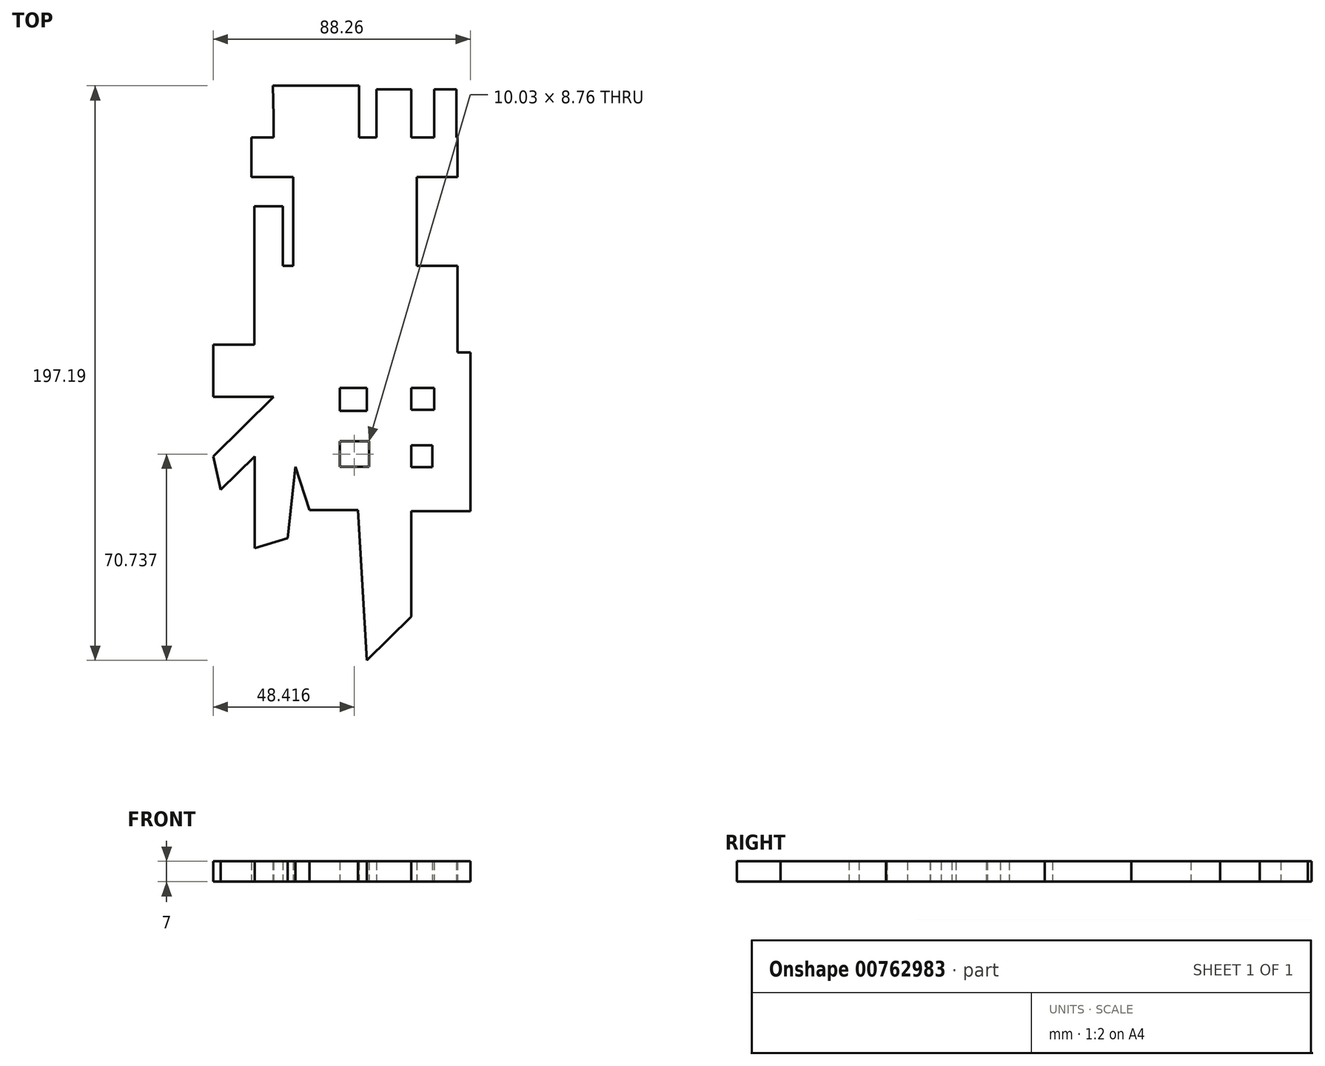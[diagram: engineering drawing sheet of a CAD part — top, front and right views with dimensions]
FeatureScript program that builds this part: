
annotation { "Feature Type Name" : "Feature", "Feature Type Description" : "" }
export const myFeature = defineFeature(function(context is Context, id is Id, definition is map)
    precondition{}
    {
        {
            var Q0;
            Q0=qCreatedBy(makeId("Top.planeOp"),FACE);
            var sketch = newSketch(context, id + "F0", { "sketchPlane" : qUnion([Q0])});
            skSolve(sketch);
        }
        {
            var Q0;
            Q0=qCreatedBy(makeId("Top.planeOp"),FACE);
            var sketch = newSketch(context, id + "F1", { "sketchPlane" : qUnion([Q0])});
            skLineSegment(sketch, "E0", {"start": v(-41.92, 16.1) * mm, "end": v(-3.32, 16.1) * mm});
            skLineSegment(sketch, "E1", {"start": v(-3.32, 16.1) * mm, "end": v(-3.32, 27.06) * mm});
            skLineSegment(sketch, "E2", {"start": v(-3.32, 27.06) * mm, "end": v(-14.67, 27.06) * mm});
            skLineSegment(sketch, "E3", {"start": v(-14.67, 27.06) * mm, "end": v(-14.67, 34.84) * mm});
            skLineSegment(sketch, "E4", {"start": v(-14.67, 34.84) * mm, "end": v(-3.32, 34.84) * mm});
            skLineSegment(sketch, "E5", {"start": v(-3.32, 34.84) * mm, "end": v(-3.32, 47.5) * mm});
            skLineSegment(sketch, "E6", {"start": v(-3.32, 47.5) * mm, "end": v(-14.67, 47.5) * mm});
            skLineSegment(sketch, "E7", {"start": v(-14.67, 47.5) * mm, "end": v(-14.67, 57.55) * mm});
            skLineSegment(sketch, "E8", {"start": v(-14.67, 57.55) * mm, "end": v(0, 57.55) * mm});
            skLineSegment(sketch, "E9", {"start": v(0, 57.55) * mm, "end": v(0, 16.1) * mm});
            skLineSegment(sketch, "E10", {"start": v(27.83, 18.3) * mm, "end": v(27.83, 27.06) * mm});
            skLineSegment(sketch, "E11", {"start": v(27.83, 27.06) * mm, "end": v(13.88, 27.06) * mm});
            skLineSegment(sketch, "E12", {"start": v(13.88, 27.06) * mm, "end": v(13.88, 57.55) * mm});
            skLineSegment(sketch, "E13", {"start": v(13.88, 57.55) * mm, "end": v(27.83, 57.55) * mm});
            skLineSegment(sketch, "E14", {"start": v(27.83, 57.55) * mm, "end": v(27.83, 71.18) * mm});
            skLineSegment(sketch, "E15", {"start": v(27.83, 71.18) * mm, "end": v(11.93, 71.18) * mm});
            skLineSegment(sketch, "E16", {"start": v(11.93, 71.18) * mm, "end": v(11.93, 87.72) * mm});
            skLineSegment(sketch, "E17", {"start": v(11.93, 87.72) * mm, "end": v(0, 87.72) * mm});
            skLineSegment(sketch, "E18", {"start": v(0, 87.72) * mm, "end": v(0, 71.18) * mm});
            skLineSegment(sketch, "E19", {"start": v(0, 71.18) * mm, "end": v(-42.9, 71.18) * mm});
            skLineSegment(sketch, "E20", {"start": v(-42.9, 71.18) * mm, "end": v(-42.9, 57.55) * mm});
            skLineSegment(sketch, "E21", {"start": v(-42.9, 57.55) * mm, "end": v(-28.62, 57.55) * mm});
            skLineSegment(sketch, "E22", {"start": v(-28.62, 57.55) * mm, "end": v(-28.62, 27.06) * mm});
            skLineSegment(sketch, "E23", {"start": v(-28.62, 27.06) * mm, "end": v(-32.19, 27.06) * mm});
            skLineSegment(sketch, "E24", {"start": v(-32.19, 27.06) * mm, "end": v(-32.19, 47.5) * mm});
            skLineSegment(sketch, "E25", {"start": v(-32.19, 47.5) * mm, "end": v(-41.92, 47.5) * mm});
            skLineSegment(sketch, "E26", {"start": v(-41.92, 47.5) * mm, "end": v(-41.92, 16.1) * mm});
            skLineSegment(sketch, "E27", {"start": v(0, 16.1) * mm, "end": v(27.83, 16.1) * mm});
            skLineSegment(sketch, "E28", {"start": v(27.83, 18.3) * mm, "end": v(27.83, 16.1) * mm});
            skLineSegment(sketch, "E29", {"start": v(-35.28, 78.46) * mm, "end": v(-6.02, 78.46) * mm});
            skLineSegment(sketch, "E30", {"start": v(-6.02, 78.46) * mm, "end": v(-6.02, 88.9) * mm});
            skLineSegment(sketch, "E31", {"start": v(-6.02, 88.9) * mm, "end": v(-35.63, 88.9) * mm});
            skLineSegment(sketch, "E32", {"start": v(19.76, 87.72) * mm, "end": v(19.76, 77.06) * mm});
            skLineSegment(sketch, "E33", {"start": v(19.76, 77.06) * mm, "end": v(27.42, 77.06) * mm});
            skLineSegment(sketch, "E34", {"start": v(27.42, 77.06) * mm, "end": v(27.42, 87.72) * mm});
            skLineSegment(sketch, "E35", {"start": v(27.42, 87.72) * mm, "end": v(19.76, 87.72) * mm});
            skLineSegment(sketch, "E36", {"start": v(-35.63, 88.9) * mm, "end": v(-35.28, 78.46) * mm});
            skLineSegment(sketch, "E37", {"start": v(-56.05, -17.86) * mm, "end": v(-35.28, -17.86) * mm});
            skLineSegment(sketch, "E38", {"start": v(-56.05, -38.25) * mm, "end": v(-35.28, -17.86) * mm});
            skLineSegment(sketch, "E39", {"start": v(-56.05, -38.25) * mm, "end": v(-53.45, -49.74) * mm});
            skLineSegment(sketch, "E40", {"start": v(-53.45, -49.74) * mm, "end": v(-41.75, -38.25) * mm});
            skLineSegment(sketch, "E41", {"start": v(-41.75, -38.25) * mm, "end": v(-41.75, -69.76) * mm});
            skLineSegment(sketch, "E42", {"start": v(-41.75, -69.76) * mm, "end": v(-30.47, -66.42) * mm});
            skLineSegment(sketch, "E43", {"start": v(-30.47, -66.42) * mm, "end": v(-27.84, -41.92) * mm});
            skLineSegment(sketch, "E44", {"start": v(-27.84, -41.92) * mm, "end": v(-23.03, -56.75) * mm});
            skLineSegment(sketch, "E45", {"start": v(-23.03, -56.75) * mm, "end": v(-6.35, -56.75) * mm});
            skLineSegment(sketch, "E46", {"start": v(-6.35, -56.75) * mm, "end": v(-3.32, -108.28) * mm});
            skLineSegment(sketch, "E47", {"start": v(-3.32, -108.28) * mm, "end": v(11.93, -93.3) * mm});
            skLineSegment(sketch, "E48", {"start": v(11.93, -93.3) * mm, "end": v(11.93, -57.12) * mm});
            skLineSegment(sketch, "E49", {"start": v(11.93, -57.12) * mm, "end": v(32.2, -57.12) * mm});
            skLineSegment(sketch, "E50", {"start": v(32.2, -57.12) * mm, "end": v(32.2, -2.63) * mm});
            skLineSegment(sketch, "E51", {"start": v(32.2, -2.63) * mm, "end": v(11.93, -2.63) * mm});
            skLineSegment(sketch, "E52", {"start": v(11.93, -2.63) * mm, "end": v(11.93, 12.57) * mm});
            skLineSegment(sketch, "E53", {"start": v(11.93, 12.57) * mm, "end": v(-3.32, 12.57) * mm});
            skLineSegment(sketch, "E54", {"start": v(-3.32, 12.57) * mm, "end": v(-3.32, 0) * mm});
            skLineSegment(sketch, "E55", {"start": v(-3.32, 0) * mm, "end": v(-56.05, 0) * mm});
            skLineSegment(sketch, "E56", {"start": v(-56.05, 0) * mm, "end": v(-56.05, -17.86) * mm});
            skLineSegment(sketch, "E57", {"start": v(-12.65, -14.86) * mm, "end": v(-12.65, -22.65) * mm});
            skLineSegment(sketch, "E58", {"start": v(-12.65, -22.65) * mm, "end": v(-3.32, -22.65) * mm});
            skLineSegment(sketch, "E59", {"start": v(-3.32, -22.65) * mm, "end": v(-3.32, -14.86) * mm});
            skLineSegment(sketch, "E60", {"start": v(-3.32, -14.86) * mm, "end": v(-12.65, -14.86) * mm});
            skLineSegment(sketch, "E61", {"start": v(-9.04, -41.92) * mm, "end": v(-3.32, -41.92) * mm});
            skLineSegment(sketch, "E62", {"start": v(-12.65, -34.51) * mm, "end": v(-12.65, -38.25) * mm});
            skLineSegment(sketch, "E63", {"start": v(11.93, -38.25) * mm, "end": v(11.93, -41.92) * mm});
            skLineSegment(sketch, "E64", {"start": v(11.93, -14.86) * mm, "end": v(11.93, -22.28) * mm});
            skLineSegment(sketch, "E65", {"start": v(11.93, -22.28) * mm, "end": v(19.76, -22.28) * mm});
            skLineSegment(sketch, "E66", {"start": v(19.76, -22.28) * mm, "end": v(19.76, -14.86) * mm});
            skLineSegment(sketch, "E67", {"start": v(19.76, -14.86) * mm, "end": v(11.93, -14.86) * mm});
            skLineSegment(sketch, "E68.bottom", {"start": v(-12.65, -33.16) * mm, "end": v(-2.62, -33.16) * mm});
            skLineSegment(sketch, "E68.top", {"start": v(-12.65, -41.92) * mm, "end": v(-2.62, -41.92) * mm});
            skLineSegment(sketch, "E68.left", {"start": v(-12.65, -33.16) * mm, "end": v(-12.65, -41.92) * mm});
            skLineSegment(sketch, "E68.right", {"start": v(-2.62, -33.16) * mm, "end": v(-2.62, -41.92) * mm});
            skLineSegment(sketch, "E69.bottom", {"start": v(11.93, -34.51) * mm, "end": v(19.21, -34.51) * mm});
            skLineSegment(sketch, "E69.top", {"start": v(11.93, -42) * mm, "end": v(19.21, -42) * mm});
            skLineSegment(sketch, "E69.left", {"start": v(11.93, -34.51) * mm, "end": v(11.93, -42) * mm});
            skLineSegment(sketch, "E69.right", {"start": v(19.21, -34.51) * mm, "end": v(19.21, -42) * mm});
            skPoint(sketch, "E69.middle", {"position": v(15.57, -38.25) * mm});
            skLineSegment(sketch, "E70", {"start": v(-41.92, 16.1) * mm, "end": v(-41.92, 0) * mm});
            skLineSegment(sketch, "E71", {"start": v(-41.92, 0) * mm, "end": v(-3.32, 0) * mm});
            skLineSegment(sketch, "E72", {"start": v(-3.32, 16.1) * mm, "end": v(-3.32, 0) * mm});
            skLineSegment(sketch, "E73", {"start": v(27.83, 16.1) * mm, "end": v(27.83, -2.63) * mm});
            skLineSegment(sketch, "E74", {"start": v(27.83, -2.63) * mm, "end": v(11.93, -2.63) * mm});
            skLineSegment(sketch, "E75", {"start": v(-35.28, 78.46) * mm, "end": v(-35.28, 71.18) * mm});
            skLineSegment(sketch, "E76", {"start": v(-35.28, 71.18) * mm, "end": v(-6.02, 71.18) * mm});
            skLineSegment(sketch, "E77", {"start": v(-6.02, 71.18) * mm, "end": v(-6.02, 78.46) * mm});
            skLineSegment(sketch, "E78", {"start": v(19.76, 77.06) * mm, "end": v(19.76, 71.18) * mm});
            skLineSegment(sketch, "E79", {"start": v(19.76, 71.18) * mm, "end": v(27.42, 71.18) * mm});
            skLineSegment(sketch, "E80", {"start": v(27.42, 71.18) * mm, "end": v(27.42, 77.06) * mm});
            skSolve(sketch);
        }
        {
            var Q0;
            Q0 = qSketchRegion(id + "F1", true);
            var Q1;
            Q1 = qSketchRegion(id + "FDJ1Ys171cJaEn7_0", true);
            var Q2;
            Q2 = qSketchRegion(id + "F0", true);
            extrude(context, id + "F2", {"entities" : qUnion([Q0, Q1, Q2]), "depth" : 7 * mm, "offsetDistance" : 25 * mm});
        }
    });
